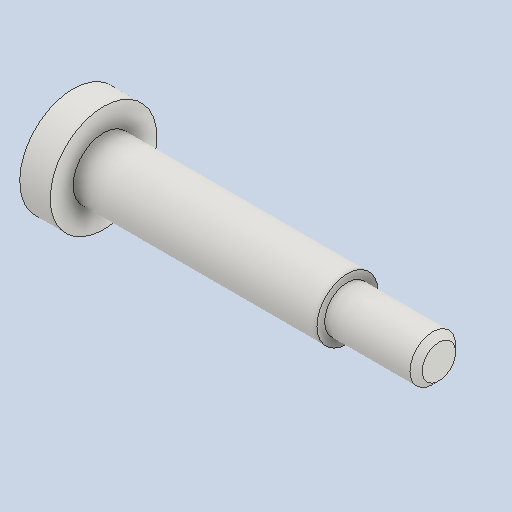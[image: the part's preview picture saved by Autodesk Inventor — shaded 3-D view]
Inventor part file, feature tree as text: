
AUTODESK INVENTOR PART (.ipt)
format: ipt  version: 2022 (Build 260153000, 153)  size: 120,320 bytes
history: native  units: mm
features: other x4, revolve x1, chamfer x1
ambient origin geometry x6: Origin, XZ Plane, XY Plane, X Axis, Y Axis, Z Axis
bodies: Body1 (feature_tree)
feature tree (6):
  other  "Твердое тело1"
  revolve  "Вращение1"
  chamfer  "Фаска1"  [1 undecoded]
  other  "Начальная плоскость"
  other  "Исходная точка"
  other  "Основной эскиз"
note: 1 required parameter value undecoded (feature->parameter linkage not recoverable at this tier; creation-order binding heuristic only, values carry confidence <= 0.55)
